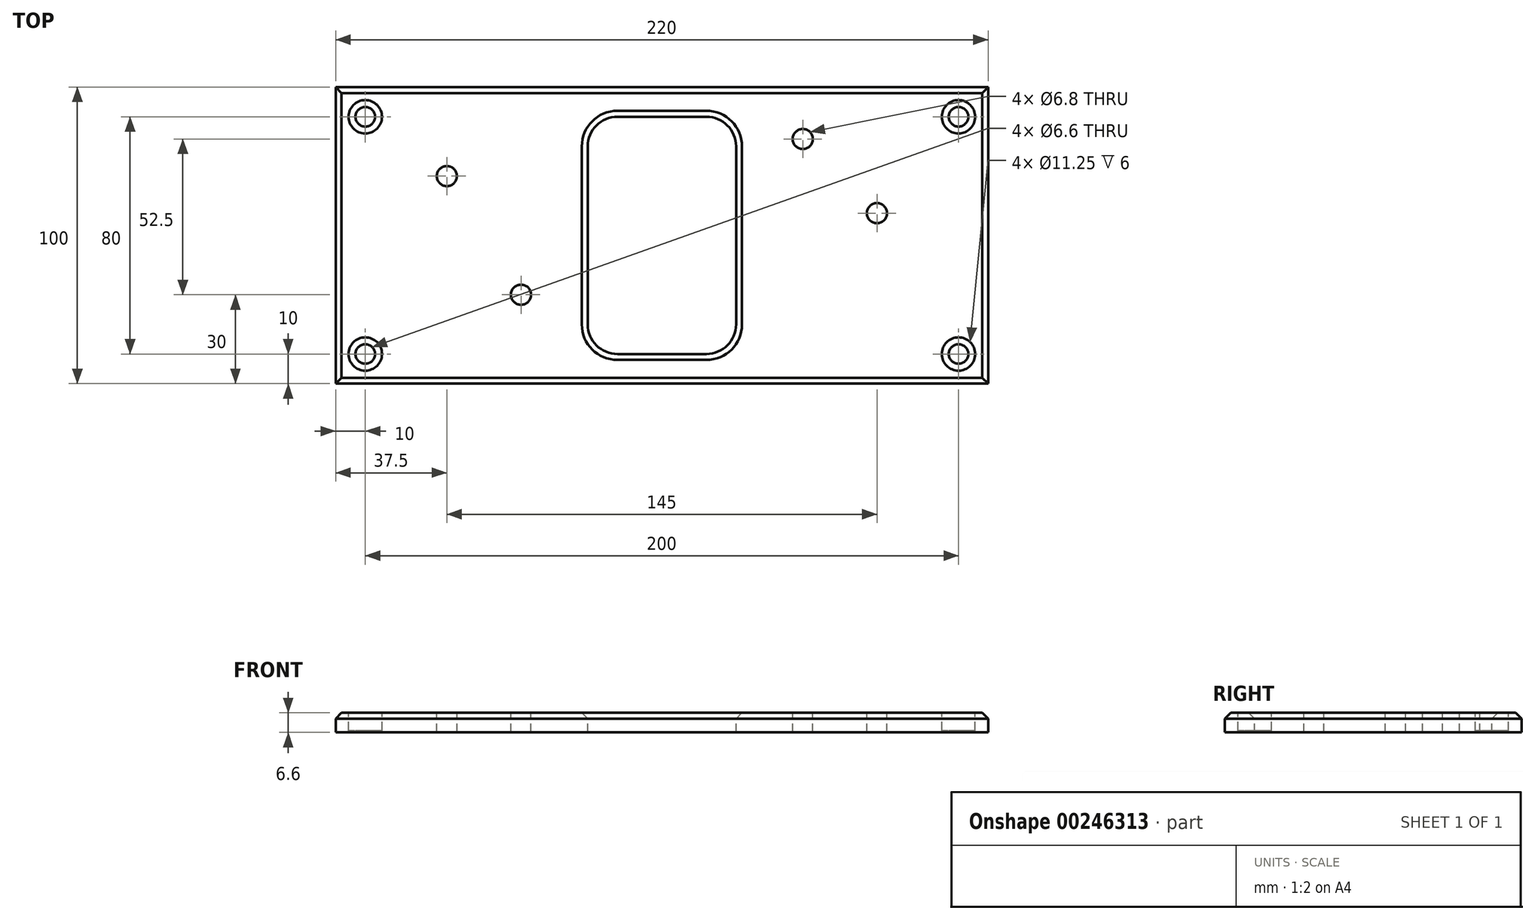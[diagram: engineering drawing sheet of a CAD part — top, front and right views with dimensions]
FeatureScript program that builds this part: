
annotation { "Feature Type Name" : "Feature", "Feature Type Description" : "" }
export const myFeature = defineFeature(function(context is Context, id is Id, definition is map)
    precondition{}
    {
        {
            var Q0;
            Q0=qCreatedBy(makeId("Top.planeOp"),FACE);
            var sketch = newSketch(context, id + "F0", { "sketchPlane" : qUnion([Q0])});
            skLineSegment(sketch, "E0.bottom", {"start": v(0, 0) * mm, "end": v(-220, 0) * mm});
            skLineSegment(sketch, "E0.top", {"start": v(0, -100) * mm, "end": v(-220, -100) * mm});
            skLineSegment(sketch, "E0.left", {"start": v(0, 0) * mm, "end": v(0, -100) * mm});
            skLineSegment(sketch, "E0.right", {"start": v(-220, 0) * mm, "end": v(-220, -100) * mm});
            skPoint(sketch, "E1", {"position": v(-182.5, -30) * mm});
            skPoint(sketch, "E2", {"position": v(-157.5, -70) * mm});
            skPoint(sketch, "E3", {"position": v(-62.5, -17.5) * mm});
            skPoint(sketch, "E4", {"position": v(-37.5, -42.5) * mm});
            skPoint(sketch, "E5.middle", {"position": v(-110, -50) * mm});
            skPoint(sketch, "E5.middle.positionSnap0", {"position": v(0, -50) * mm});
            skPoint(sketch, "E5.middle.positionSnap1", {"position": v(-110, 0) * mm});
            skPoint(sketch, "E5.centerSnap0", {"position": v(0, -50) * mm});
            skPoint(sketch, "E5.centerSnap1", {"position": v(-110, 0) * mm});
            skCircle(sketch, "E6", {"center": v(-182.5, -30) * mm, "radius": 0.63 * mm});
            skCircle(sketch, "E7", {"center": v(-157.5, -70) * mm, "radius": 0.62 * mm});
            skCircle(sketch, "E8", {"center": v(-37.5, -42.5) * mm, "radius": 0.63 * mm});
            skCircle(sketch, "E9", {"center": v(-62.5, -17.5) * mm, "radius": 0.63 * mm});
            skLineSegment(sketch, "E10.bottom", {"start": v(-135, -10) * mm, "end": v(-85, -10) * mm});
            skLineSegment(sketch, "E10.top", {"start": v(-135, -90) * mm, "end": v(-85, -90) * mm});
            skLineSegment(sketch, "E10.left", {"start": v(-135, -10) * mm, "end": v(-135, -90) * mm});
            skLineSegment(sketch, "E10.right", {"start": v(-85, -10) * mm, "end": v(-85, -90) * mm});
            skPoint(sketch, "E11", {"position": v(-210, -10) * mm});
            skPoint(sketch, "E12", {"position": v(-210, -90) * mm});
            skPoint(sketch, "E13", {"position": v(-10, -10) * mm});
            skPoint(sketch, "E14", {"position": v(-10, -90) * mm});
            skSolve(sketch);
        }
        {
            var Q0;
            Q0=makeQuery(id+"F0.imprint","IMPRINT",FACE,{"disambiguationData":[TD([[makeQuery(id+"F0.imprint","IMPRINT",EDGE,{"derivedFrom":sQuery(id+"F0.wireOp",EDGE,"KF58jQ8D-vqHp-ix9u-DEfj-FtAcLMWgaiPX")}),1.0]])]});
            var Q1;
            Q1=makeQuery(id+"F0.imprint","IMPRINT",FACE,{"disambiguationData":[TD([[makeQuery(id+"F0.imprint","IMPRINT",EDGE,{"derivedFrom":sQuery(id+"F0.wireOp",EDGE,"mKvIFw0l-cJgm-kAc4-Qajh-wdcZaxDhrAz0")}),1.0]])]});
            var Q2;
            Q2=makeQuery(id+"F0.imprint","IMPRINT",FACE,{"disambiguationData":[TD([[makeQuery(id+"F0.imprint","IMPRINT",EDGE,{"derivedFrom":sQuery(id+"F0.wireOp",EDGE,"FN07gYyd-EOgK-WMpG-ySna-u93LrKOQSkwO")}),1.0]])]});
            var Q3;
            Q3=makeQuery(id+"F0.imprint","IMPRINT",FACE,{"disambiguationData":[TD([[makeQuery(id+"F0.imprint","IMPRINT",EDGE,{"derivedFrom":sQuery(id+"F0.wireOp",EDGE,"yshLCDdg-VlSO-vuOb-TDv7-KXUFp9xids6u")}),1.0]])]});
            var Q4;
            Q4=makeQuery(id+"F0.imprint","IMPRINT",FACE,{"disambiguationData":[TD([[makeQuery(id+"F0.imprint","IMPRINT",EDGE,{"derivedFrom":sQuery(id+"F0.wireOp",EDGE,"E0.bottom")}),1.0]])]});
            extrude(context, id + "F1", {"entities" : qUnion([Q0, Q1, Q2, Q3, Q4]), "oppositeDirection" : true, "depth" : 6.6 * mm});
        }
        {
            var Q0;
            Q0=makeQuery(id+"F1.opExtrude","CAP_EDGE",EDGE,{"disambiguationData":[OSD([sQuery(id+"F0.wireOp",EDGE,"E5.bottom")])],"isStart":true});
            var Q1;
            Q1=makeQuery(id+"F1.opExtrude","CAP_EDGE",EDGE,{"disambiguationData":[OSD([sQuery(id+"F0.wireOp",EDGE,"E0.top")])],"isStart":true});
            var Q2;
            Q2=makeQuery(id+"F1.opExtrude","CAP_EDGE",EDGE,{"disambiguationData":[OSD([sQuery(id+"F0.wireOp",EDGE,"E0.left")])],"isStart":true});
            var Q3;
            Q3=makeQuery(id+"F1.opExtrude","CAP_EDGE",EDGE,{"disambiguationData":[OSD([sQuery(id+"F0.wireOp",EDGE,"E0.bottom")])],"isStart":true});
            var Q4;
            Q4=makeQuery(id+"F1.opExtrude","CAP_EDGE",EDGE,{"disambiguationData":[OSD([sQuery(id+"F0.wireOp",EDGE,"E0.right")])],"isStart":true});
            chamfer(context, id + "F2", {"entities" : qUnion([Q0, Q1, Q2, Q3, Q4]), "chamferType" : ChamferType.OFFSET_ANGLE, "width" : 2 * mm, "oppositeDirection" : false, "angle" : 45 * degree, "tangentPropagation" : true});
        }
        {
            var Q0;
            Q0=sQuery(id+"F0.wireOp",VERTEX,"E1");
            var Q1;
            Q1=sQuery(id+"F0.wireOp",VERTEX,"E2");
            var Q2;
            Q2=sQuery(id+"F0.wireOp",VERTEX,"E4");
            var Q3;
            Q3=sQuery(id+"F0.wireOp",VERTEX,"E3");
            var Q4;
            Q4=makeQuery(id+"F1.opExtrude","SWEPT_BODY",BODY,{"disambiguationData":[OSD([sQuery(id+"F0.wireOp",EDGE,"E0.bottom"),sQuery(id+"F0.wireOp",EDGE,"E0.top"),sQuery(id+"F0.wireOp",EDGE,"E0.left"),sQuery(id+"F0.wireOp",EDGE,"E0.right"),sQuery(id+"F0.wireOp",EDGE,"E6"),sQuery(id+"F0.wireOp",EDGE,"E7"),sQuery(id+"F0.wireOp",EDGE,"E8"),sQuery(id+"F0.wireOp",EDGE,"E9"),sQuery(id+"F0.wireOp",EDGE,"a9d0DtRW-2sf6-uEDk-i2r7-7SJeso2GBNUJ"),sQuery(id+"F0.wireOp",EDGE,"v2LYcekk-PA2R-tv3Q-ZGHl-xQntgVUS5d7g"),sQuery(id+"F0.wireOp",EDGE,"qpZ91wCh-UkYP-FIzR-fegP-7RP9dC3F6s4o"),sQuery(id+"F0.wireOp",EDGE,"GuOmbg3c-PAG3-KNyk-SRzR-5WI8BxOXNmej"),sQuery(id+"F0.wireOp",EDGE,"E10.bottom"),sQuery(id+"F0.wireOp",EDGE,"E10.top"),sQuery(id+"F0.wireOp",EDGE,"E10.left"),sQuery(id+"F0.wireOp",EDGE,"E10.right")])]});
            hole(context, id + "F3", {"style" : HoleStyle.SIMPLE, "endStyle" : HoleEndStyle.THROUGH, "standardTappedOrClearance" : lookupTablePath({ "standard" : "ISO", "engagement" : "75%", "pitch" : "1.25 mm", "size" : "M8", "type" : "Tapped" }), "standardBlindInLast" : lookupTablePath({ "standard" : "ISO", "engagement" : "75%", "pitch" : "1.25 mm", "size" : "M8", "type" : "Tapped" }), "holeDiameter" : 6.8 * mm, "showTappedDepth" : true, "tappedDepth" : 12 * mm, "tapClearance" : 3, "locations" : qUnion([Q0, Q1, Q2, Q3]), "scope" : qUnion([Q4]), "majorDiameter" : 8 * mm});
        }
        {
            var Q0;
            Q0=sQuery(id+"F0.wireOp",VERTEX,"E11");
            var Q1;
            Q1=sQuery(id+"F0.wireOp",VERTEX,"E12");
            var Q2;
            Q2=sQuery(id+"F0.wireOp",VERTEX,"E14");
            var Q3;
            Q3=sQuery(id+"F0.wireOp",VERTEX,"E13");
            var Q4;
            Q4=makeQuery(id+"F1.opExtrude","SWEPT_BODY",BODY,{"disambiguationData":[OSD([sQuery(id+"F0.wireOp",EDGE,"E0.bottom"),sQuery(id+"F0.wireOp",EDGE,"E0.top"),sQuery(id+"F0.wireOp",EDGE,"E0.left"),sQuery(id+"F0.wireOp",EDGE,"E0.right"),sQuery(id+"F0.wireOp",EDGE,"E6"),sQuery(id+"F0.wireOp",EDGE,"E7"),sQuery(id+"F0.wireOp",EDGE,"E8"),sQuery(id+"F0.wireOp",EDGE,"E9"),sQuery(id+"F0.wireOp",EDGE,"E10.bottom"),sQuery(id+"F0.wireOp",EDGE,"E10.top"),sQuery(id+"F0.wireOp",EDGE,"E10.left"),sQuery(id+"F0.wireOp",EDGE,"E10.right")])]});
            hole(context, id + "F4", {"style" : HoleStyle.C_BORE, "endStyle" : HoleEndStyle.THROUGH, "holeDiameter" : 6.6 * mm, "cBoreDiameter" : 11.25 * mm, "cBoreDepth" : 6 * mm, "tappedDepth" : 12 * mm, "tapClearance" : 3, "locations" : qUnion([Q0, Q1, Q2, Q3]), "scope" : qUnion([Q4])});
        }
        {
            var Q0;
            Q0=makeQuery(id+"F1.opExtrude","SWEPT_EDGE",EDGE,{"disambiguationData":[OSD([sQuery(id+"F0.wireOp",EDGE,"E10.bottom"),sQuery(id+"F0.wireOp",EDGE,"E10.left")])]});
            var Q1;
            Q1=makeQuery(id+"F1.opExtrude","SWEPT_EDGE",EDGE,{"disambiguationData":[OSD([sQuery(id+"F0.wireOp",EDGE,"E10.bottom"),sQuery(id+"F0.wireOp",EDGE,"E10.right")])]});
            var Q2;
            Q2=makeQuery(id+"F1.opExtrude","SWEPT_EDGE",EDGE,{"disambiguationData":[OSD([sQuery(id+"F0.wireOp",EDGE,"E10.top"),sQuery(id+"F0.wireOp",EDGE,"E10.left")])]});
            var Q3;
            Q3=makeQuery(id+"F1.opExtrude","SWEPT_EDGE",EDGE,{"disambiguationData":[OSD([sQuery(id+"F0.wireOp",EDGE,"E10.top"),sQuery(id+"F0.wireOp",EDGE,"E10.right")])]});
            fillet(context, id + "F5", {"entities" : qUnion([Q0, Q1, Q2, Q3]), "radius" : 10 * mm, "tangentPropagation" : true, "allowEdgeOverflow" : false});
        }
        {
            var Q0;
            Q0=makeQuery(id+"F1.opExtrude","CAP_EDGE",EDGE,{"disambiguationData":[OSD([sQuery(id+"F0.wireOp",EDGE,"E10.left")])],"isStart":true});
            chamfer(context, id + "F6", {"entities" : qUnion([Q0]), "chamferType" : ChamferType.OFFSET_ANGLE, "width" : 2 * mm, "oppositeDirection" : false, "angle" : 45 * degree, "tangentPropagation" : true});
        }
    });
